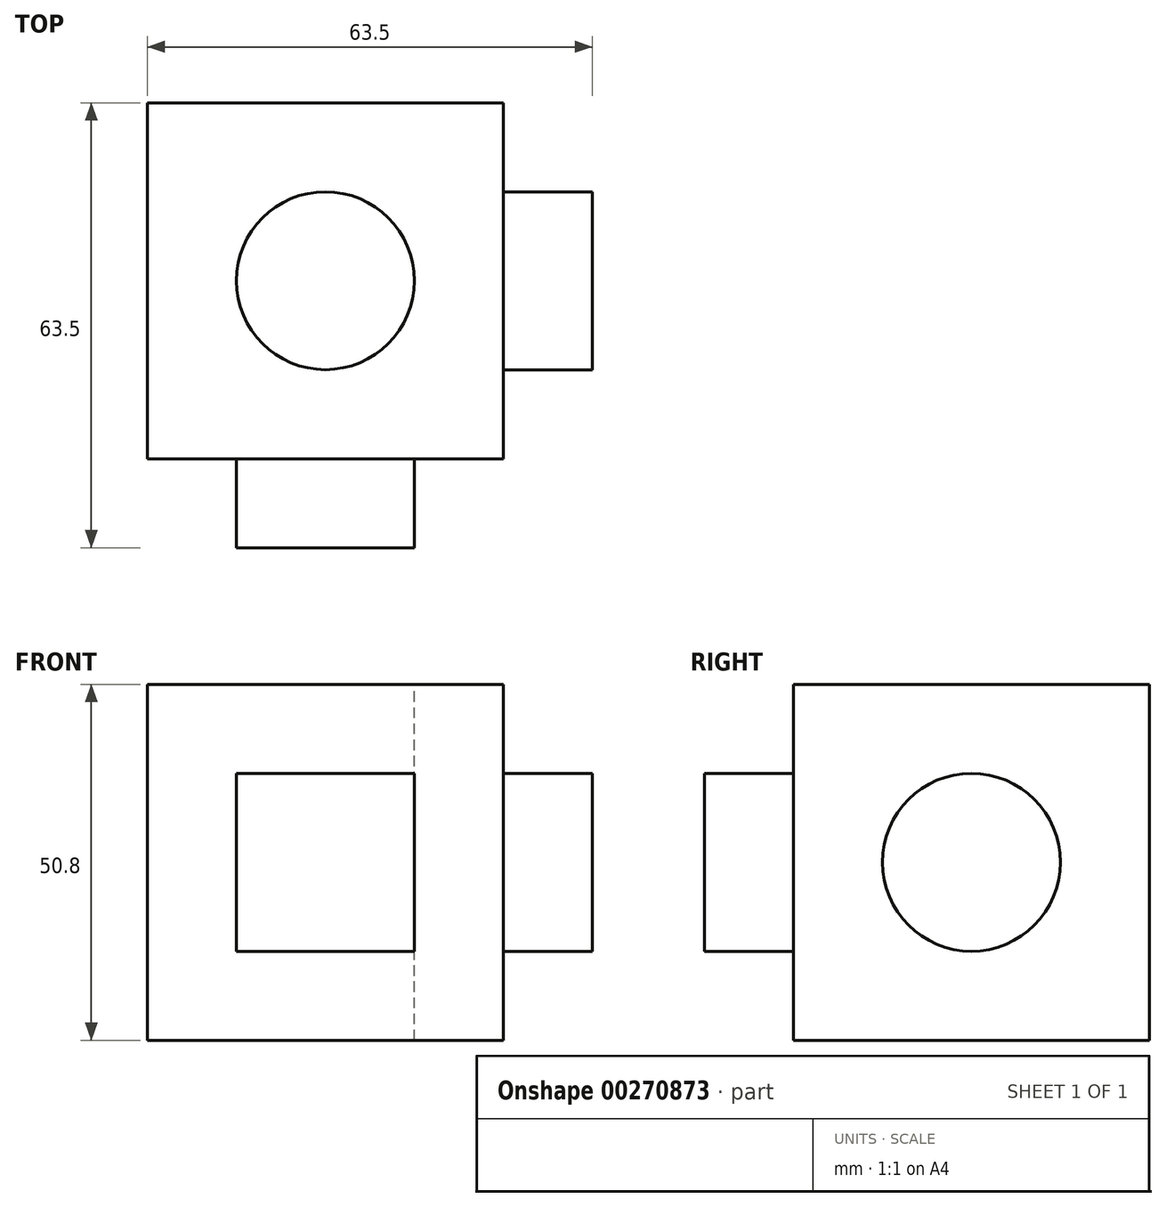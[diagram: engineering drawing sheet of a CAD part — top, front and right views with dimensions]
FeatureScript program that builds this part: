
annotation { "Feature Type Name" : "Feature", "Feature Type Description" : "" }
export const myFeature = defineFeature(function(context is Context, id is Id, definition is map)
    precondition{}
    {
        {
            var Q0;
            Q0=qCreatedBy(makeId("Front.planeOp"),FACE);
            var sketch = newSketch(context, id + "F0", { "sketchPlane" : qUnion([Q0])});
            skLineSegment(sketch, "E0.bottom", {"start": v(0, 0) * mm, "end": v(-50.8, 0) * mm});
            skLineSegment(sketch, "E0.top", {"start": v(0, 50.8) * mm, "end": v(-50.8, 50.8) * mm});
            skLineSegment(sketch, "E0.left", {"start": v(0, 0) * mm, "end": v(0, 50.8) * mm});
            skLineSegment(sketch, "E0.right", {"start": v(-50.8, 0) * mm, "end": v(-50.8, 50.8) * mm});
            skSolve(sketch);
        }
        {
            var Q0;
            Q0 = qSketchRegion(id + "F0", true);
            extrude(context, id + "F1", {"entities" : qUnion([Q0]), "depth" : 50.8 * mm});
        }
        {
            var Q0;
            Q0=makeQuery(id+"F1.opExtrude","SWEPT_FACE",FACE,{"disambiguationData":[OSD([sQuery(id+"F0.wireOp",EDGE,"E0.top")])]});
            var sketch = newSketch(context, id + "F2", { "sketchPlane" : qUnion([Q0])});
            skCircle(sketch, "E1", {"center": v(-25.4, -25.4) * mm, "radius": 12.7 * mm});
            skSolve(sketch);
        }
        {
            var Q0;
            Q0 = qSketchRegion(id + "F2", true);
            extrude(context, id + "F3", {"entities" : qUnion([Q0]), "operationType" : NewBodyOperationType.REMOVE, "oppositeDirection" : true, "depth" : 50.8 * mm});
        }
        {
            var Q0;
            Q0=makeQuery(id+"F1.opExtrude","CAP_FACE",FACE,{"disambiguationData":[OSD([sQuery(id+"F0.wireOp",EDGE,"E0.bottom"),sQuery(id+"F0.wireOp",EDGE,"E0.top"),sQuery(id+"F0.wireOp",EDGE,"E0.left"),sQuery(id+"F0.wireOp",EDGE,"E0.right")])],"isStart":false});
            var sketch = newSketch(context, id + "F4", { "sketchPlane" : qUnion([Q0])});
            skLineSegment(sketch, "E2.bottom", {"start": v(-12.7, 12.7) * mm, "end": v(-38.1, 12.7) * mm});
            skLineSegment(sketch, "E2.top", {"start": v(-12.7, 38.1) * mm, "end": v(-38.1, 38.1) * mm});
            skLineSegment(sketch, "E2.left", {"start": v(-12.7, 12.7) * mm, "end": v(-12.7, 38.1) * mm});
            skLineSegment(sketch, "E2.right", {"start": v(-38.1, 12.7) * mm, "end": v(-38.1, 38.1) * mm});
            skSolve(sketch);
        }
        {
            var Q0;
            Q0 = qSketchRegion(id + "F4", true);
            extrude(context, id + "F5", {"entities" : qUnion([Q0]), "operationType" : NewBodyOperationType.ADD, "depth" : 12.7 * mm});
        }
        {
            var Q0;
            Q0=makeQuery(id+"F1.opExtrude","SWEPT_FACE",FACE,{"disambiguationData":[OSD([sQuery(id+"F0.wireOp",EDGE,"E0.left")])]});
            var sketch = newSketch(context, id + "F6", { "sketchPlane" : qUnion([Q0])});
            skCircle(sketch, "E3", {"center": v(-25.4, 25.4) * mm, "radius": 12.7 * mm});
            skSolve(sketch);
        }
        {
            var Q0;
            Q0 = qSketchRegion(id + "F6", true);
            extrude(context, id + "F7", {"entities" : qUnion([Q0]), "operationType" : NewBodyOperationType.ADD, "depth" : 12.7 * mm});
        }
    });
